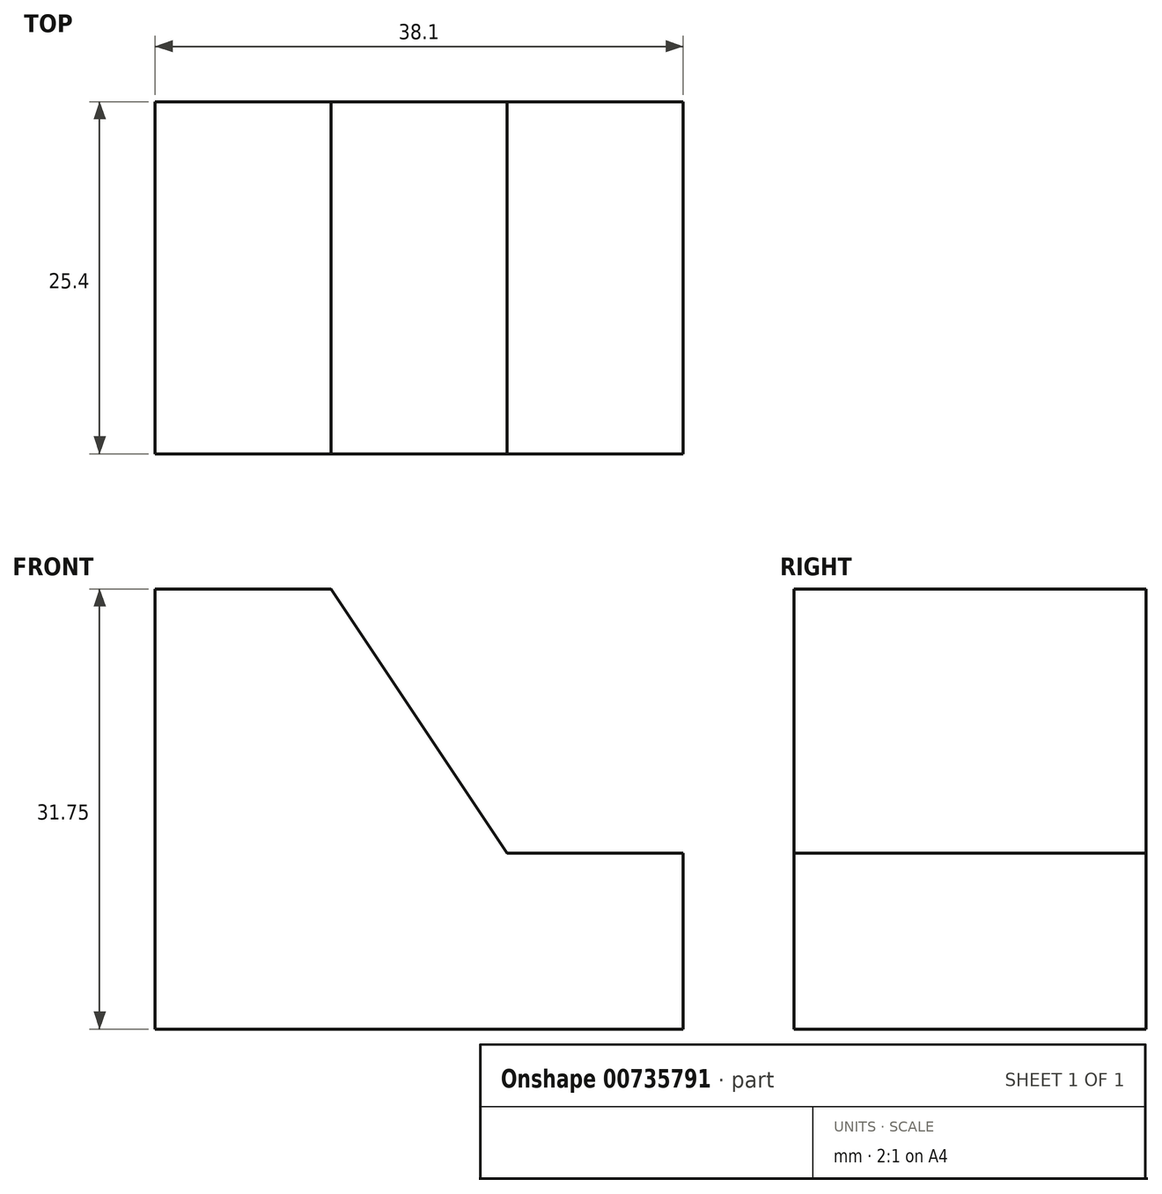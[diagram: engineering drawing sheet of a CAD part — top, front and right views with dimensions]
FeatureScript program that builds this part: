
annotation { "Feature Type Name" : "Feature", "Feature Type Description" : "" }
export const myFeature = defineFeature(function(context is Context, id is Id, definition is map)
    precondition{}
    {
        {
            var Q0;
            Q0=qCreatedBy(makeId("Front.planeOp"),FACE);
            var sketch = newSketch(context, id + "F0", { "sketchPlane" : qUnion([Q0])});
            skLineSegment(sketch, "E0", {"start": v(0, 0) * mm, "end": v(38.1, 0) * mm});
            skLineSegment(sketch, "E1", {"start": v(38.1, 0) * mm, "end": v(38.1, 12.7) * mm});
            skLineSegment(sketch, "E2", {"start": v(38.1, 12.7) * mm, "end": v(25.4, 12.7) * mm});
            skLineSegment(sketch, "E3", {"start": v(25.4, 12.7) * mm, "end": v(12.7, 31.75) * mm});
            skLineSegment(sketch, "E4", {"start": v(12.7, 31.75) * mm, "end": v(0, 31.75) * mm});
            skLineSegment(sketch, "E5", {"start": v(0, 31.75) * mm, "end": v(0, 0) * mm});
            skSolve(sketch);
        }
        {
            var Q0;
            Q0=makeQuery(id+"F0.imprint","IMPRINT",FACE,{"disambiguationData":[TD([[makeQuery(id+"F0.imprint","IMPRINT",EDGE,{"derivedFrom":sQuery(id+"F0.wireOp",EDGE,"E0")}),1.0]])]});
            extrude(context, id + "F1", {"entities" : qUnion([Q0]), "depth" : 25.4 * mm, "offsetDistance" : 25.4 * mm});
        }
    });
